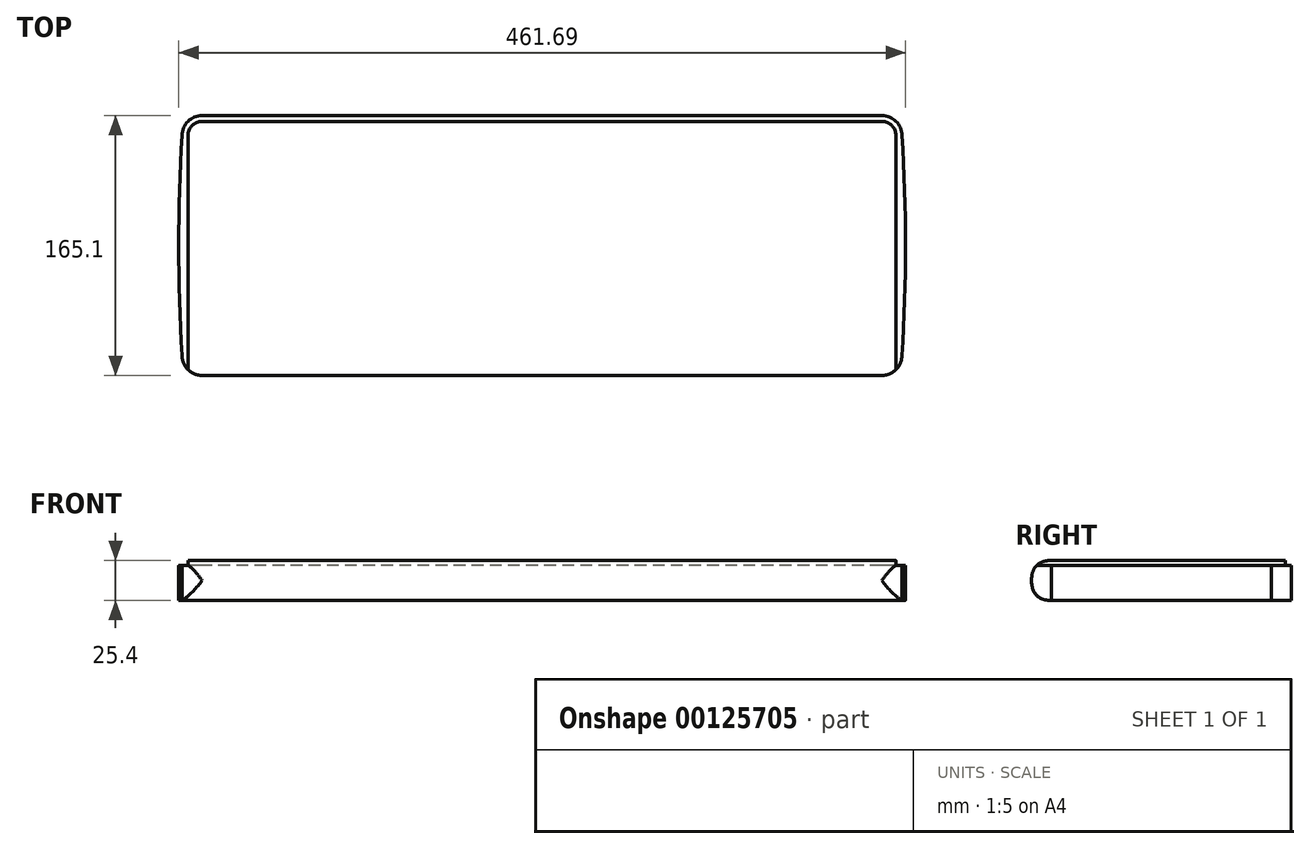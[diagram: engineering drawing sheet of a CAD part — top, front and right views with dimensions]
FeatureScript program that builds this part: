
annotation { "Feature Type Name" : "Feature", "Feature Type Description" : "" }
export const myFeature = defineFeature(function(context is Context, id is Id, definition is map)
    precondition{}
    {
        {
            var Q0;
            Q0=qCreatedBy(makeId("Top.planeOp"),FACE);
            var sketch = newSketch(context, id + "F0", { "sketchPlane" : qUnion([Q0])});
            skLineSegment(sketch, "E0.bottom", {"start": v(215.9, 82.55) * mm, "end": v(-215.9, 82.55) * mm});
            skLineSegment(sketch, "E0.top", {"start": v(215.9, -82.55) * mm, "end": v(-215.9, -82.55) * mm});
            skPoint(sketch, "E0.middle", {"position": v(0, 0) * mm});
            skPoint(sketch, "E1.visualSharp", {"position": v(-228.6, 82.55) * mm});
            skArc(sketch, "E1.filletArc", {"start": v(-215.9, 82.55) * mm, "mid": v(-224.88, 78.83) * mm, "end": v(-228.6, 69.85) * mm});
            skPoint(sketch, "E2.visualSharp", {"position": v(-228.6, -82.55) * mm});
            skArc(sketch, "E2.filletArc", {"start": v(-228.6, -69.85) * mm, "mid": v(-224.88, -78.83) * mm, "end": v(-215.9, -82.55) * mm});
            skPoint(sketch, "E3.visualSharp", {"position": v(228.6, -82.55) * mm});
            skArc(sketch, "E3.filletArc", {"start": v(215.9, -82.55) * mm, "mid": v(224.88, -78.83) * mm, "end": v(228.6, -69.85) * mm});
            skPoint(sketch, "E4.visualSharp", {"position": v(228.6, 82.55) * mm});
            skArc(sketch, "E4.filletArc", {"start": v(228.6, 69.85) * mm, "mid": v(224.88, 78.83) * mm, "end": v(215.9, 82.55) * mm});
            skLineSegment(sketch, "E5.0", {"start": v(224.8, 69.85) * mm, "end": v(224.8, -69.85) * mm});
            skArc(sketch, "E5.2", {"start": v(224.8, 69.85) * mm, "mid": v(222.19, 76.14) * mm, "end": v(215.9, 78.74) * mm});
            skLineSegment(sketch, "E5.4", {"start": v(215.9, 78.74) * mm, "end": v(-215.9, 78.74) * mm});
            skArc(sketch, "E5.5", {"start": v(-215.9, 78.74) * mm, "mid": v(-222.19, 76.14) * mm, "end": v(-224.8, 69.85) * mm});
            skLineSegment(sketch, "E5.6", {"start": v(-224.8, 69.85) * mm, "end": v(-224.79, -69.85) * mm});
            skLineSegment(sketch, "E6", {"start": v(-215.9, -82.55) * mm, "end": v(-215.9, -82.55) * mm});
            skLineSegment(sketch, "E7", {"start": v(228.6, -69.85) * mm, "end": v(228.6, -69.85) * mm});
            skLineSegment(sketch, "E8", {"start": v(224.8, -69.85) * mm, "end": v(224.8, -78.92) * mm});
            skLineSegment(sketch, "E9", {"start": v(-224.79, -69.85) * mm, "end": v(-224.79, -78.92) * mm});
            skPoint(sketch, "E10.start.orphan", {"position": v(228.6, 0) * mm});
            skPoint(sketch, "E11.start.orphan", {"position": v(-228.6, 0) * mm});
            skArc(sketch, "E12", {"start": v(-228.6, 69.85) * mm, "mid": v(-230.73, 0) * mm, "end": v(-228.6, -69.85) * mm});
            skArc(sketch, "E13", {"start": v(228.6, -69.85) * mm, "mid": v(230.96, 0) * mm, "end": v(228.6, 69.85) * mm});
            skSolve(sketch);
        }
        {
            var Q0;
            {var subQ0=sQuery(id+"F0.wireOp",EDGE,"E0.top");Q0=makeQuery(id+"F0.imprint","IMPRINT",FACE,{"disambiguationData":[TD([[makeQuery(id+"F0.imprint","IMPRINT",EDGE,{"derivedFrom":subQ0}),-1.0]])]});}
            extrude(context, id + "F1", {"entities" : qUnion([Q0]), "depth" : 25.4 * mm});
        }
        {
            var Q0;
            Q0=makeQuery(id+"F0.imprint","IMPRINT",FACE,{"disambiguationData":[TD([[makeQuery(id+"F0.imprint","IMPRINT",EDGE,{"derivedFrom":sQuery(id+"F0.wireOp",EDGE,"E0.bottom")}),1.0]])]});
            extrude(context, id + "F2", {"entities" : qUnion([Q0]), "operationType" : NewBodyOperationType.ADD, "depth" : 22.1 * mm});
        }
        {
            var Q0;
            Q0=makeQuery(id+"F1.opExtrude","SWEPT_FACE",FACE,{"disambiguationData":[OSD([sQuery(id+"F0.wireOp",EDGE,"E0.top")])]});
            fillet(context, id + "F3", {"entities" : qUnion([Q0]), "radius" : 12.7 * mm, "rho" : 0.5, "crossSection" : FilletCrossSection.CONIC, "allowEdgeOverflow" : false});
        }
        {
            var Q0;
            Q0=makeQuery(id+"F1.opExtrude","CAP_FACE",FACE,{"disambiguationData":[OSD([sQuery(id+"F0.wireOp",EDGE,"E0.top"),sQuery(id+"F0.wireOp",EDGE,"E2.filletArc"),sQuery(id+"F0.wireOp",EDGE,"E3.filletArc"),sQuery(id+"F0.wireOp",EDGE,"E5.0"),sQuery(id+"F0.wireOp",EDGE,"E5.2"),sQuery(id+"F0.wireOp",EDGE,"E5.4"),sQuery(id+"F0.wireOp",EDGE,"E5.5"),sQuery(id+"F0.wireOp",EDGE,"E5.6"),sQuery(id+"F0.wireOp",EDGE,"E8"),sQuery(id+"F0.wireOp",EDGE,"E9")])],"isStart":false});
            cPlane(context, id + "F4", {"entities" : qUnion([Q0]), "cplaneType" : CPlaneType.OFFSET, "offset" : 0 * mm, "width" : 152.4 * mm, "height" : 152.4 * mm});
        }
    });
